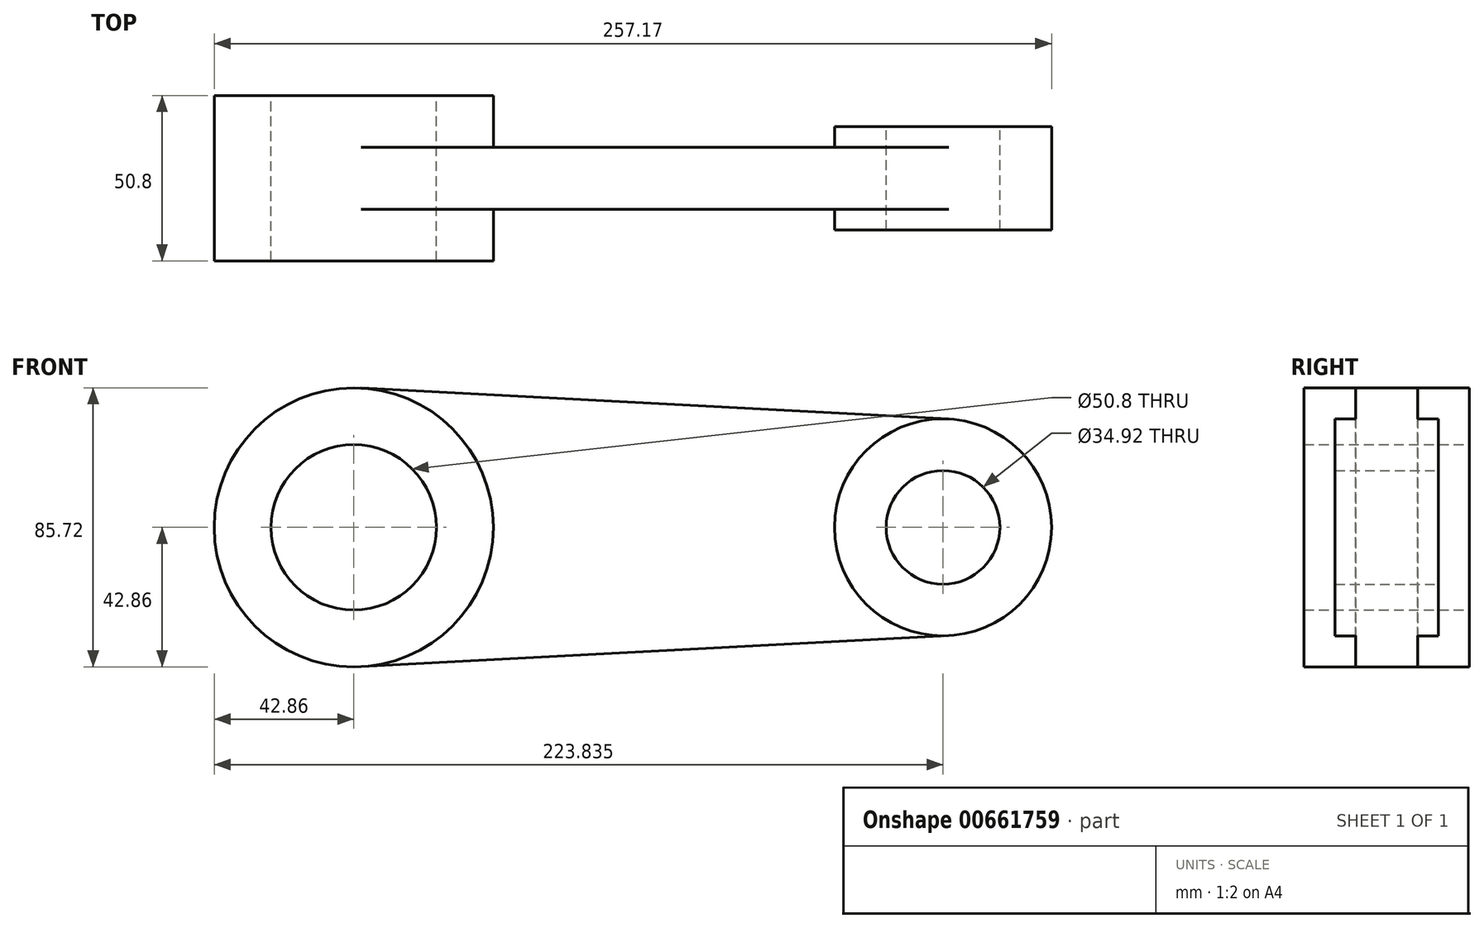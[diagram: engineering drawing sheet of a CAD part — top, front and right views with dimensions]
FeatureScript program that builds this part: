
annotation { "Feature Type Name" : "Feature", "Feature Type Description" : "" }
export const myFeature = defineFeature(function(context is Context, id is Id, definition is map)
    precondition{}
    {
        {
            var Q0;
            Q0=qCreatedBy(makeId("Front.planeOp"),FACE);
            var sketch = newSketch(context, id + "F0", { "sketchPlane" : qUnion([Q0])});
            skCircle(sketch, "E0", {"center": v(0, 0) * mm, "radius": 25.4 * mm});
            skCircle(sketch, "E1", {"center": v(0, 0) * mm, "radius": 42.86 * mm});
            skCircle(sketch, "E2", {"center": v(180.98, 0) * mm, "radius": 17.46 * mm});
            skCircle(sketch, "E3", {"center": v(180.98, 0) * mm, "radius": 33.34 * mm});
            skLineSegment(sketch, "E4", {"start": v(0, 0) * mm, "end": v(180.98, 0) * mm, "construction": true});
            skLineSegment(sketch, "E5", {"start": v(2.26, 42.8) * mm, "end": v(182.73, 33.3) * mm});
            skLineSegment(sketch, "E6.MirrorCS", {"start": v(2.26, -42.8) * mm, "end": v(182.73, -33.3) * mm});
            skSolve(sketch);
        }
        {
            var Q0;
            Q0=makeQuery(id+"F0.imprint","IMPRINT",FACE,{"disambiguationData":[TD([[makeQuery(id+"F0.imprint","IMPRINT",EDGE,{"derivedFrom":sQuery(id+"F0.wireOp",EDGE,"E0")}),-1.0]])]});
            extrude(context, id + "F1", {"entities" : qUnion([Q0]), "endBound" : BoundingType.SYMMETRIC, "depth" : 50.8 * mm});
        }
        {
            var Q0;
            {var subQ0=sQuery(id+"F0.wireOp",EDGE,"iaiyhtZe-uAdw-0OpP-Abch-S62ud13HqYB8");var subQ1=sQuery(id+"F0.wireOp",EDGE,"E1");var subQ2=makeQuery(id+"F0.imprint","INTERSECT",VERTEX,{"disambiguationData":[OD(1.0)],"derivedFrom":[subQ1,subQ0]});Q0=makeQuery(id+"F0.imprint","IMPRINT",FACE,{"disambiguationData":[TD([[makeQuery(id+"F0.imprint","IMPRINT",EDGE,{"disambiguationData":[TD([[subQ2,1.0]])],"derivedFrom":subQ1}),-1.0]])]});}
            extrude(context, id + "F2", {"entities" : qUnion([Q0]), "operationType" : NewBodyOperationType.ADD, "endBound" : BoundingType.SYMMETRIC, "depth" : 19.05 * mm});
        }
        {
            var Q0;
            Q0=makeQuery(id+"F0.imprint","IMPRINT",FACE,{"disambiguationData":[TD([[makeQuery(id+"F0.imprint","IMPRINT",EDGE,{"derivedFrom":sQuery(id+"F0.wireOp",EDGE,"E2")}),-1.0]])]});
            extrude(context, id + "F3", {"entities" : qUnion([Q0]), "operationType" : NewBodyOperationType.ADD, "endBound" : BoundingType.SYMMETRIC, "depth" : 31.75 * mm});
        }
    });
